# Revit family: CENTUM Z-Niederhalter
name_source: partatom
category: HLS-Bauteile
revit_build: Autodesk Revit 2018 (Build: 20190510_1515(x64)
units: mm (PartAtom-declared; Revit-internal decimal feet)

## family parameters
Arbeitsebenenbasiert = Ja
Beim Laden mit Abzugskörper schneiden = Nein
Bemaßung runder Anschluss = Durchmesser verwenden
Gemeinsam genutzt = Ja
Immer vertikal = Nein
Raumberechnungspunkt = Nein
Teiletyp = Normal

## types (1)
- CENTUM Z-Niederhalter
    Anzahl Befestigungsloch = 1 St
    Artikelnummer = 1650015017
    Befestigungsloch = 13 mm
    Breite = 80 mm  [stored 0.262467 ft]
    D = 11 mm
    EAN = 4250928459725
    Fabrikat = MEFA
    Firma = MEFA Befestigungs- und Montagesysteme GmbH
    Gewicht = 0.79 kg
    Gewicht pro Bauteil = 0.79 kg
    Höhe = 19.5 mm
    Kurztext1 = Niederhalter CENTUM
    Kurztext2 = max. Plattenstärke 16 mm ZnNi
    L = 80 mm  [stored 0.262467 ft]
    Länge = 70 mm  [stored 0.229659 ft]
    MD = 3 mm  [stored 0.00984252 ft]
    Material = Stahl
    Materialname = S235
    Mengeneinheit = Set
    Oberflaeche = galvanisch verzinkt
    Stärke = 0 mm  [stored 0 ft]
    Stärke Material 1 = 3 mm
    Vorgabe-Ansicht = 1219 mm
    max. Plattenstärke = 14,5 mm
    max. zul. Abhebelast (Paar) = 0.00 kN
    vpe = 1

note: [stored X ft] marks values corroborated as IEEE doubles in the binary element streams (Revit-internal decimal feet)
